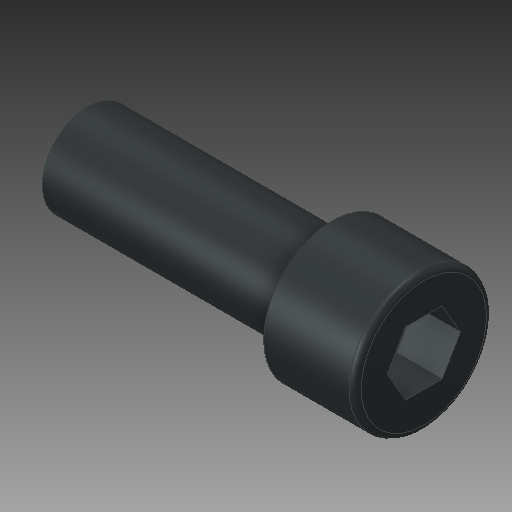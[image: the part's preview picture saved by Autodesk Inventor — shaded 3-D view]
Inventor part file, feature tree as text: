
AUTODESK INVENTOR PART (.ipt)
format: ipt  version: 2019 (Build 230136000, 136)  size: 138,240 bytes
history: native  units: mm
features: extrude x3, sketch x3, plane x1, fillet x1
ambient origin geometry x8: Origin, YZ Plane, XZ Plane, XY Plane, X Axis, Y Axis, Z Axis, Center Point
bodies: Solid1 (feature_tree)
feature tree (8):
  extrude  "Extrusion1"  Depth=8.0mm TaperAngle=0.0deg
  extrude  "Extrusion2"  Depth=3.0mm TaperAngle=0.0deg
  plane  "Work Plane1"
  fillet  "Fillet2"  Radius=0.2mm
  extrude  "Extrusion4"  Depth=1.5mm
  sketch  "Sketch1"  dims[d0=3.0mm d1=8.0mm d2=0.0mm]
  sketch  "Sketch2"  dims[d3=4.5mm d4=3.0mm d5=0.0mm d13=0.2mm]
  sketch  "Sketch4"  dims[d14=2.4mm d15=1.03923mm d16=1.5mm d17=0.0mm]
